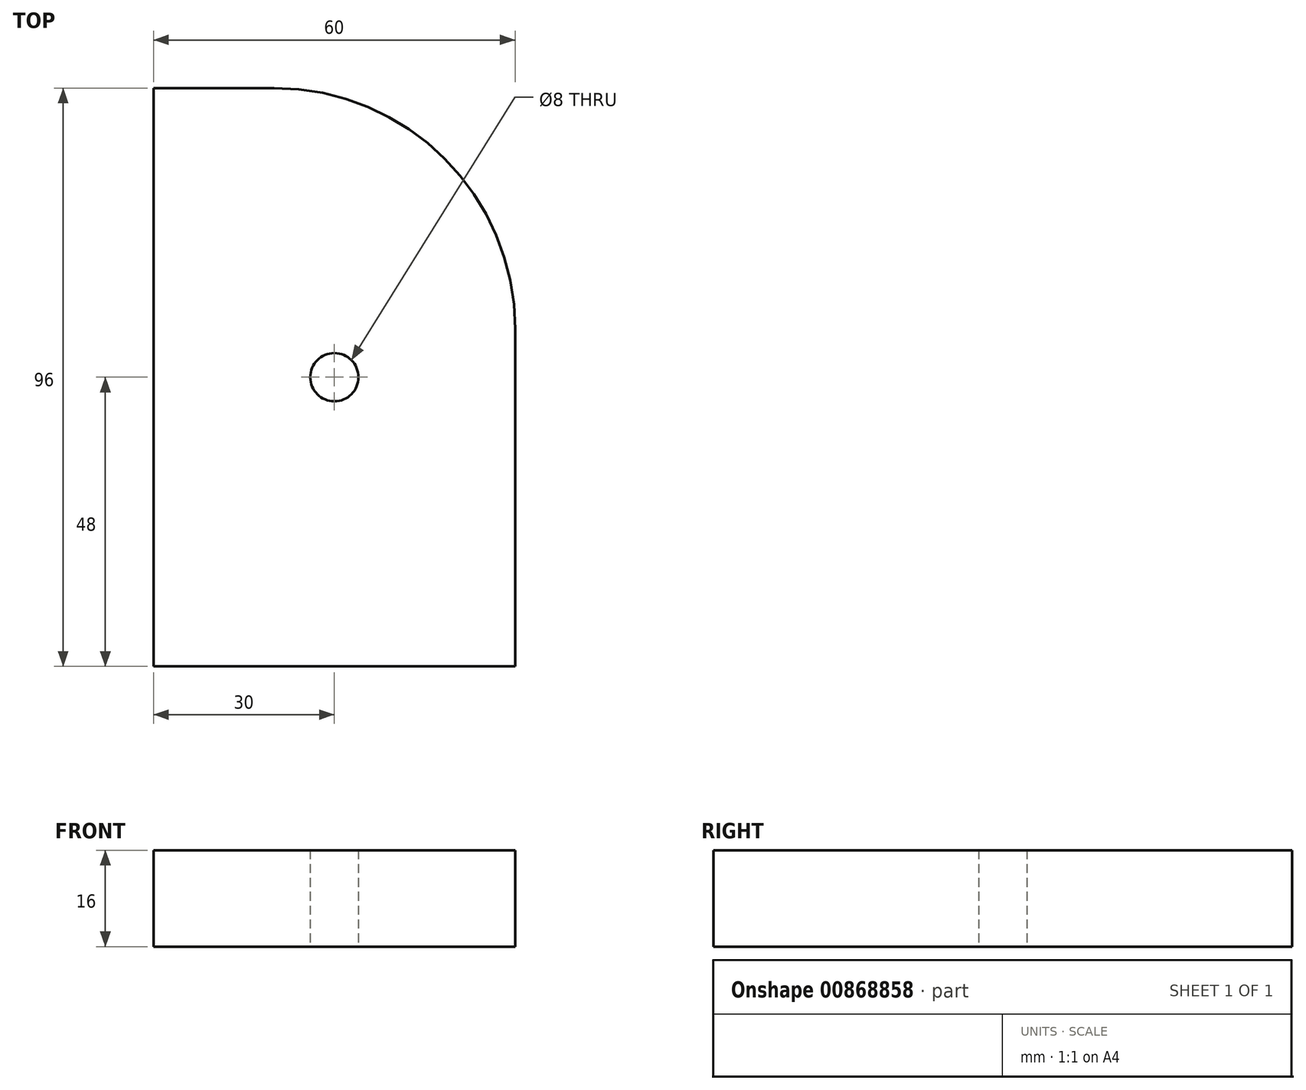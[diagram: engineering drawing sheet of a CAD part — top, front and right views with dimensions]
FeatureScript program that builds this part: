
annotation { "Feature Type Name" : "Feature", "Feature Type Description" : "" }
export const myFeature = defineFeature(function(context is Context, id is Id, definition is map)
    precondition{}
    {
        {
            var Q0;
            Q0=qCreatedBy(makeId("Top.planeOp"),FACE);
            var sketch = newSketch(context, id + "F0", { "sketchPlane" : qUnion([Q0])});
            skLineSegment(sketch, "E0.bottom", {"start": v(0, 0) * mm, "end": v(60, 0) * mm});
            skLineSegment(sketch, "E0.top", {"start": v(0, 96) * mm, "end": v(60, 96) * mm});
            skLineSegment(sketch, "E0.left", {"start": v(0, 0) * mm, "end": v(0, 96) * mm});
            skLineSegment(sketch, "E0.right", {"start": v(60, 0) * mm, "end": v(60, 96) * mm});
            skLineSegment(sketch, "E1", {"start": v(30, 0) * mm, "end": v(30, 96) * mm});
            skLineSegment(sketch, "E2", {"start": v(0, 48) * mm, "end": v(60, 48) * mm});
            skCircle(sketch, "E3", {"center": v(30, 48) * mm, "radius": 4 * mm});
            skSolve(sketch);
        }
        {
            var Q0;
            {var subQ1=sQuery(id+"F0.wireOp",EDGE,"E0.top");var subQ5=sQuery(id+"F0.wireOp",EDGE,"E0.left");var subQ6=makeQuery(id+"F0.imprint","INTERSECT",VERTEX,{"derivedFrom":[subQ1,subQ5]});Q0=makeQuery(id+"F0.imprint","IMPRINT",FACE,{"disambiguationData":[TD([[makeQuery(id+"F0.imprint","IMPRINT",EDGE,{"disambiguationData":[TD([[subQ6,-1.0]])],"derivedFrom":subQ1}),-1.0]])]});}
            var Q1;
            {var subQ1=sQuery(id+"F0.wireOp",EDGE,"E0.right");var subQ6=sQuery(id+"F0.wireOp",EDGE,"E0.top");var subQ9=makeQuery(id+"F0.imprint","INTERSECT",VERTEX,{"derivedFrom":[subQ6,subQ1]});Q1=makeQuery(id+"F0.imprint","IMPRINT",FACE,{"disambiguationData":[TD([[makeQuery(id+"F0.imprint","IMPRINT",EDGE,{"disambiguationData":[TD([[subQ9,1.0]])],"derivedFrom":subQ6}),-1.0]])]});}
            var Q2;
            {var subQ1=sQuery(id+"F0.wireOp",EDGE,"E0.right");var subQ6=sQuery(id+"F0.wireOp",EDGE,"E0.bottom");var subQ9=makeQuery(id+"F0.imprint","INTERSECT",VERTEX,{"derivedFrom":[subQ6,subQ1]});Q2=makeQuery(id+"F0.imprint","IMPRINT",FACE,{"disambiguationData":[TD([[makeQuery(id+"F0.imprint","IMPRINT",EDGE,{"disambiguationData":[TD([[subQ9,1.0]])],"derivedFrom":subQ6}),1.0]])]});}
            var Q3;
            {var subQ1=sQuery(id+"F0.wireOp",EDGE,"E0.left");var subQ6=sQuery(id+"F0.wireOp",EDGE,"E0.bottom");var subQ9=makeQuery(id+"F0.imprint","INTERSECT",VERTEX,{"derivedFrom":[subQ6,subQ1]});Q3=makeQuery(id+"F0.imprint","IMPRINT",FACE,{"disambiguationData":[TD([[makeQuery(id+"F0.imprint","IMPRINT",EDGE,{"disambiguationData":[TD([[subQ9,-1.0]])],"derivedFrom":subQ6}),1.0]])]});}
            extrude(context, id + "F1", {"entities" : qUnion([Q0, Q1, Q2, Q3]), "depth" : 16 * mm, "offsetDistance" : 25 * mm});
        }
        {
            var Q0;
            Q0=makeQuery(id+"F1.opExtrude","SWEPT_EDGE",EDGE,{"disambiguationData":[OSD([sQuery(id+"F0.wireOp",EDGE,"E0.top"),sQuery(id+"F0.wireOp",EDGE,"E0.right")])]});
            fillet(context, id + "F2", {"entities" : qUnion([Q0]), "radius" : 40 * mm, "tangentPropagation" : true, "allowEdgeOverflow" : false});
        }
    });
